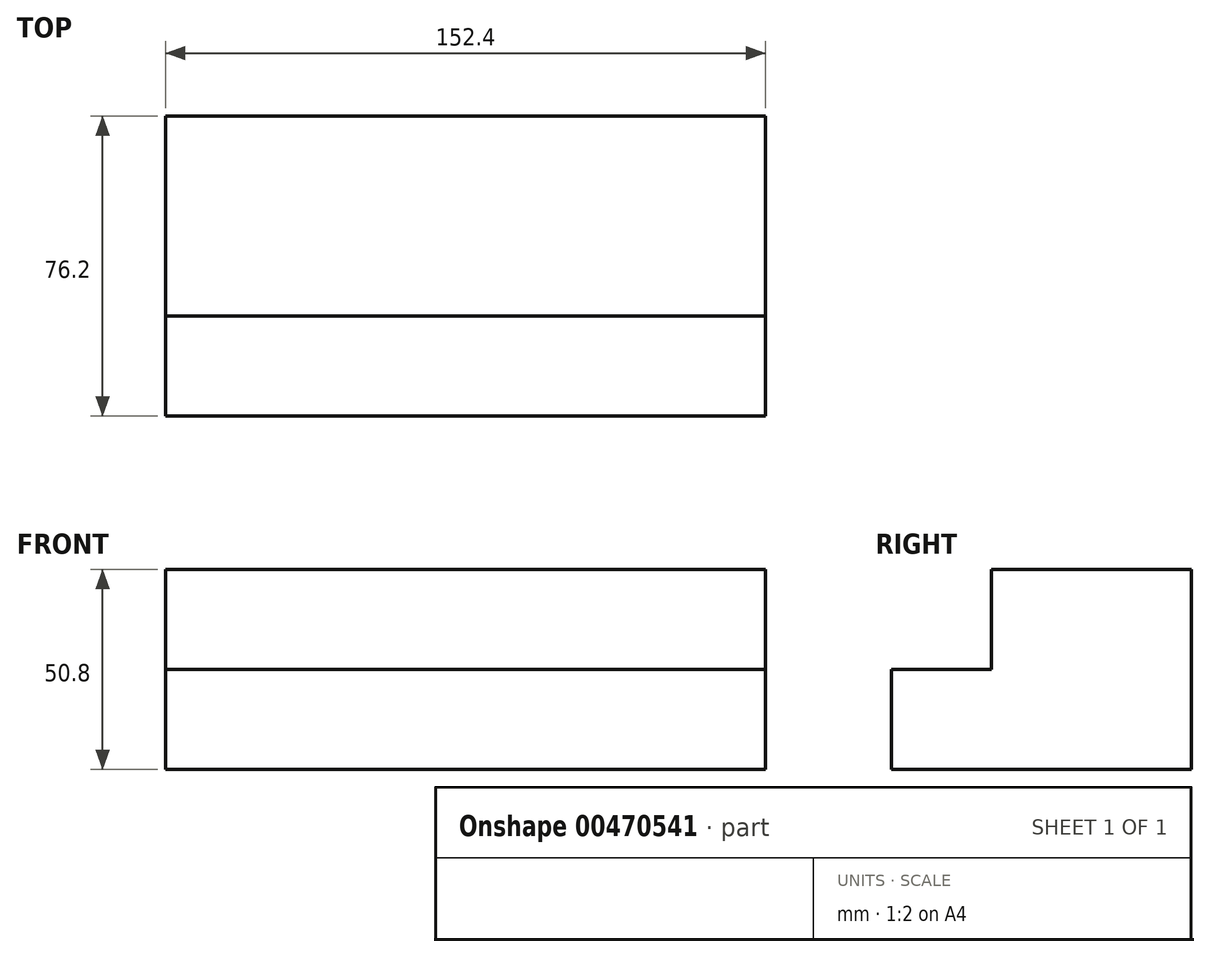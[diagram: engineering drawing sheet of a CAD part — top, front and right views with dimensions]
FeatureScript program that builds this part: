
annotation { "Feature Type Name" : "Feature", "Feature Type Description" : "" }
export const myFeature = defineFeature(function(context is Context, id is Id, definition is map)
    precondition{}
    {
        {
            var Q0;
            Q0=qCreatedBy(makeId("Right.planeOp"),FACE);
            var sketch = newSketch(context, id + "F0", { "sketchPlane" : qUnion([Q0])});
            skLineSegment(sketch, "E0", {"start": v(51.18, 28.57) * mm, "end": v(0.38, 28.57) * mm});
            skLineSegment(sketch, "E1", {"start": v(0.38, 28.57) * mm, "end": v(0.38, 3.17) * mm});
            skLineSegment(sketch, "E2", {"start": v(0.38, 3.17) * mm, "end": v(-25.02, 3.17) * mm});
            skLineSegment(sketch, "E3", {"start": v(-25.02, 3.17) * mm, "end": v(-25.02, -22.23) * mm});
            skLineSegment(sketch, "E4", {"start": v(-25.02, -22.23) * mm, "end": v(51.18, -22.23) * mm});
            skLineSegment(sketch, "E5", {"start": v(51.18, -22.23) * mm, "end": v(51.18, 28.57) * mm});
            skSolve(sketch);
        }
        {
            var Q0;
            Q0 = qSketchRegion(id + "F0", true);
            extrude(context, id + "F1", {"entities" : qUnion([Q0]), "depth" : 152.4 * mm});
        }
    });
